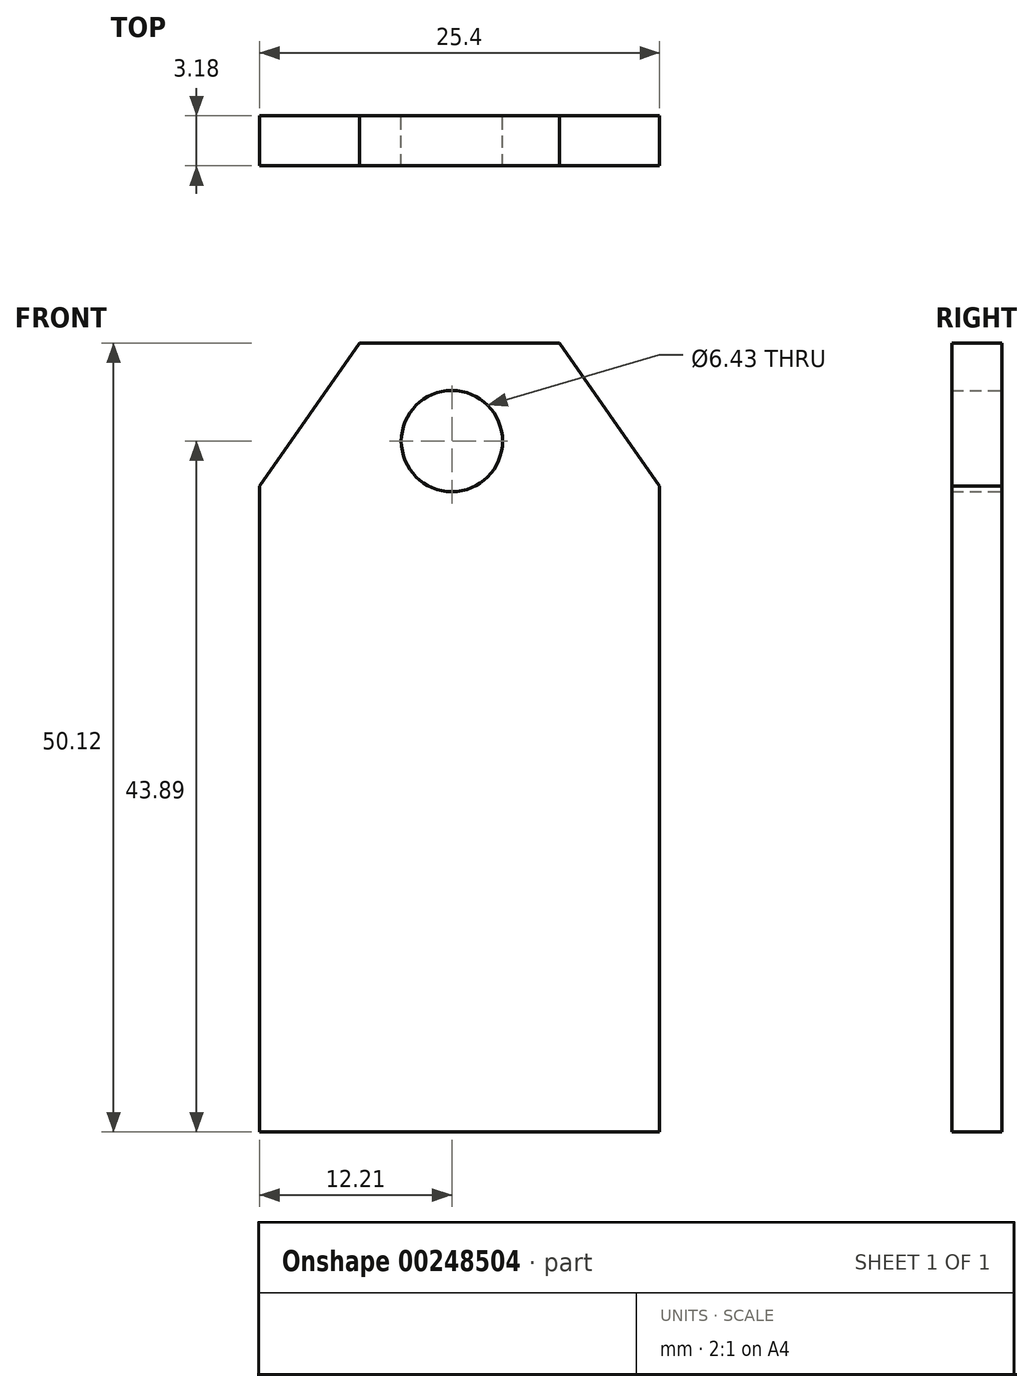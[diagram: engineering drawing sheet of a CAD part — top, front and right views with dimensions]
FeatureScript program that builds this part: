
annotation { "Feature Type Name" : "Feature", "Feature Type Description" : "" }
export const myFeature = defineFeature(function(context is Context, id is Id, definition is map)
    precondition{}
    {
        {
            var Q0;
            Q0=qCreatedBy(makeId("Front.planeOp"),FACE);
            var sketch = newSketch(context, id + "F0", { "sketchPlane" : qUnion([Q0])});
            skLineSegment(sketch, "E0", {"start": v(0, 0) * mm, "end": v(-25.4, 0) * mm});
            skLineSegment(sketch, "E1", {"start": v(-25.4, 0) * mm, "end": v(-25.4, 41.05) * mm});
            skLineSegment(sketch, "E2", {"start": v(-25.4, 41.05) * mm, "end": v(-19.05, 50.12) * mm});
            skLineSegment(sketch, "E3", {"start": v(-19.05, 50.12) * mm, "end": v(-6.35, 50.12) * mm});
            skLineSegment(sketch, "E4", {"start": v(-6.35, 50.12) * mm, "end": v(0, 41.05) * mm});
            skLineSegment(sketch, "E5", {"start": v(0, 41.05) * mm, "end": v(0, 0) * mm});
            skCircle(sketch, "E6", {"center": v(-13.19, 43.9) * mm, "radius": 3.22 * mm});
            skSolve(sketch);
        }
        {
            var Q0;
            Q0 = qSketchRegion(id + "F0", true);
            extrude(context, id + "F1", {"entities" : qUnion([Q0]), "depth" : 3.17 * mm});
        }
    });
